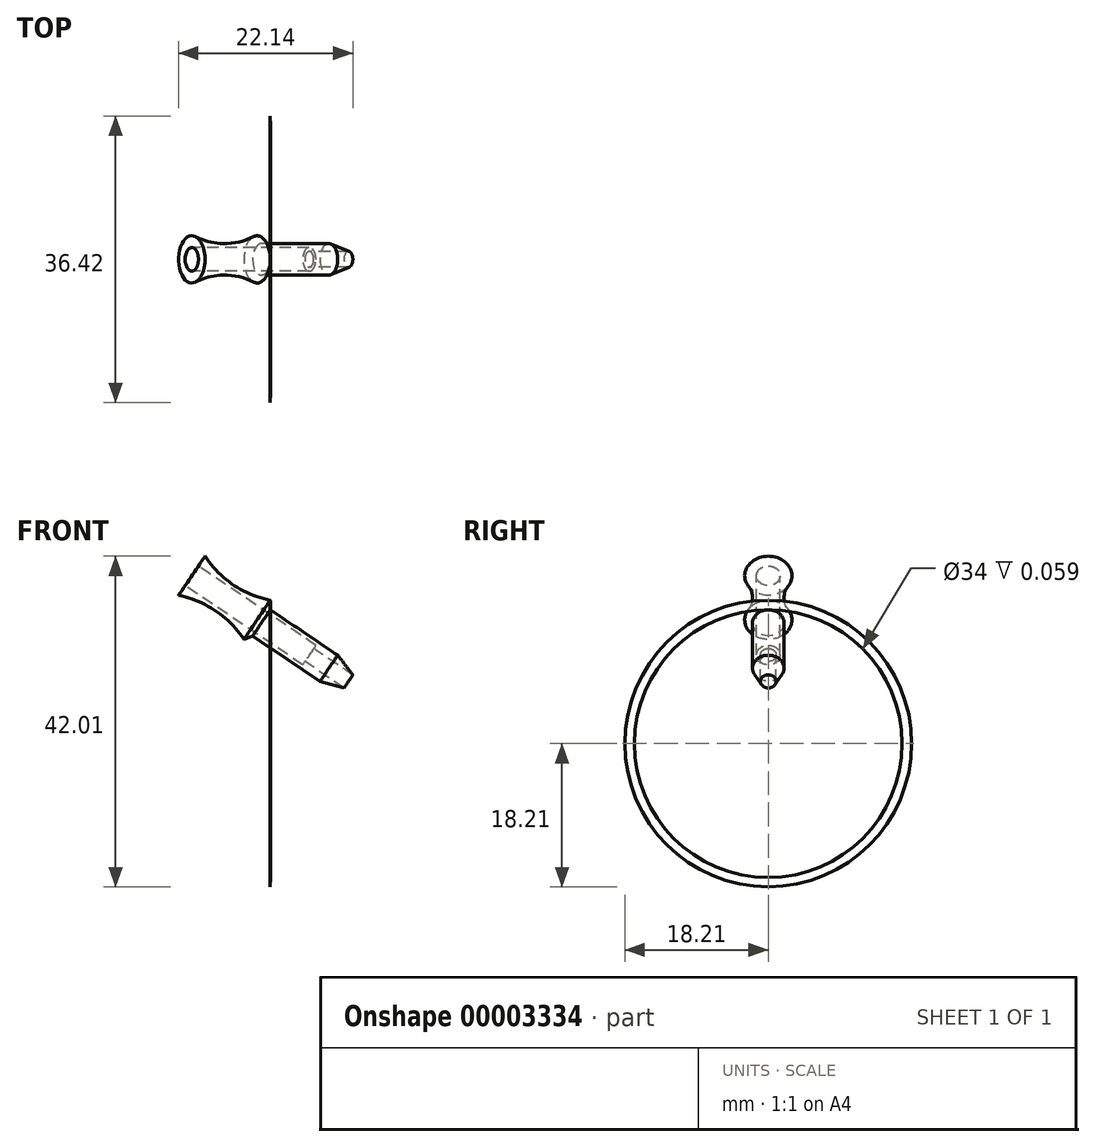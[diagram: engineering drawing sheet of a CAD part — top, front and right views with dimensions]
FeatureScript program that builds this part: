
annotation { "Feature Type Name" : "Feature", "Feature Type Description" : "" }
export const myFeature = defineFeature(function(context is Context, id is Id, definition is map)
    precondition{}
    {
        {
            var Q0;
            Q0=qCreatedBy(makeId("Front.planeOp"),FACE);
            var sketch = newSketch(context, id + "F0", { "sketchPlane" : qUnion([Q0])});
            skLineSegment(sketch, "E0", {"start": v(0, 0) * mm, "end": v(7.5, 0) * mm, "construction": true});
            skLineSegment(sketch, "E1", {"start": v(0, 17) * mm, "end": v(0, 20.5) * mm});
            skLineSegment(sketch, "E2", {"start": v(0, 20.5) * mm, "end": v(7.5, 20.5) * mm});
            skLineSegment(sketch, "E3.0.MirrorCS", {"start": v(0, -17) * mm, "end": v(0, -20.5) * mm});
            skLineSegment(sketch, "E4.0.MirrorCS", {"start": v(0, -20.5) * mm, "end": v(7.5, -20.5) * mm});
            skLineSegment(sketch, "E5.0", {"start": v(1.5, 18.9) * mm, "end": v(7.5, 18.9) * mm});
            skLineSegment(sketch, "E5.1", {"start": v(1.5, 17) * mm, "end": v(1.5, 18.9) * mm});
            skLineSegment(sketch, "E6.0.MirrorCS", {"start": v(1.5, -17) * mm, "end": v(1.5, -18.9) * mm});
            skLineSegment(sketch, "E7.0.MirrorCS", {"start": v(1.5, -18.9) * mm, "end": v(7.5, -18.9) * mm});
            skLineSegment(sketch, "E8", {"start": v(0, 17) * mm, "end": v(1.5, 17) * mm});
            skLineSegment(sketch, "E9", {"start": v(7.5, 20.5) * mm, "end": v(7.5, 18.9) * mm});
            skLineSegment(sketch, "E10.0.MirrorCS", {"start": v(0, -17) * mm, "end": v(1.5, -17) * mm});
            skLineSegment(sketch, "E11.0.MirrorCS", {"start": v(7.5, -20.5) * mm, "end": v(7.5, -18.9) * mm});
            skLineSegment(sketch, "E12", {"start": v(-9.97, 21.31) * mm, "end": v(10, 7.84) * mm, "construction": true});
            skLineSegment(sketch, "E13", {"start": v(-9.13, 22.55) * mm, "end": v(-8.3, 23.8) * mm});
            skLineSegment(sketch, "E14", {"start": v(0, 18.2) * mm, "end": v(0, 17) * mm});
            skLineSegment(sketch, "E15", {"start": v(0, 17) * mm, "end": v(8.56, 11.23) * mm});
            skLineSegment(sketch, "E16", {"start": v(8.56, 11.23) * mm, "end": v(10.49, 8.72) * mm});
            skLineSegment(sketch, "E17", {"start": v(-9.13, 22.55) * mm, "end": v(5.8, 12.49) * mm});
            skArc(sketch, "E18", {"start": v(-8.3, 23.8) * mm, "mid": v(-4.7, 20.17) * mm, "end": v(0, 18.2) * mm});
            skLineSegment(sketch, "E19", {"start": v(-8.3, 23.8) * mm, "end": v(0, 18.2) * mm, "construction": true});
            skLineSegment(sketch, "E20", {"start": v(8.56, 11.23) * mm, "end": v(8, 10.4) * mm, "construction": true});
            skLineSegment(sketch, "E21", {"start": v(10.49, 8.72) * mm, "end": v(5.51, 12.07) * mm});
            skLineSegment(sketch, "E22", {"start": v(5.51, 12.07) * mm, "end": v(5.8, 12.49) * mm});
            skLineSegment(sketch, "E23.0.MirrorCS", {"start": v(9.37, 7.06) * mm, "end": v(4.4, 10.42) * mm});
            skLineSegment(sketch, "E24.0.MirrorCS", {"start": v(6.32, 7.9) * mm, "end": v(9.37, 7.06) * mm});
            skLineSegment(sketch, "E25.0.MirrorCS", {"start": v(-2.24, 13.68) * mm, "end": v(6.32, 7.9) * mm});
            skLineSegment(sketch, "E26.0.MirrorCS", {"start": v(4.12, 10) * mm, "end": v(4.4, 10.42) * mm});
            skLineSegment(sketch, "E27.0.MirrorCS", {"start": v(-10.8, 20.07) * mm, "end": v(4.12, 10) * mm});
            skLineSegment(sketch, "E28.0.MirrorCS", {"start": v(-3.36, 13.23) * mm, "end": v(-2.24, 13.68) * mm});
            skArc(sketch, "E29.0.MirrorCS", {"start": v(-11.65, 18.82) * mm, "mid": v(-6.94, 16.86) * mm, "end": v(-3.36, 13.23) * mm});
            skLineSegment(sketch, "E30.0.MirrorCS", {"start": v(-10.8, 20.07) * mm, "end": v(-11.65, 18.82) * mm});
            skLineSegment(sketch, "E31", {"start": v(0, 18.2) * mm, "end": v(0.06, 16.96) * mm});
            skSolve(sketch);
        }
        {
            var Q0;
            {var subQ3=sQuery(id+"F0.wireOp",EDGE,"E1");Q0=makeQuery(id+"F0.imprint","IMPRINT",FACE,{"disambiguationData":[TD([[makeQuery(id+"F0.imprint","IMPRINT",EDGE,{"derivedFrom":subQ3}),-1.0]])]});}
            var Q1;
            {var subQ3=sQuery(id+"F0.wireOp",EDGE,"E14");Q1=makeQuery(id+"F0.imprint","IMPRINT",FACE,{"disambiguationData":[TD([[makeQuery(id+"F0.imprint","IMPRINT",EDGE,{"derivedFrom":subQ3}),1.0]])]});}
            var Q2;
            Q2=sQuery(id+"F0.wireOp",EDGE,"E0");
            revolve(context, id + "F1", {"entities" : qUnion([Q0, Q1]), "axis" : qUnion([Q2]), "revolveType" : RevolveType.FULL});
        }
        {
            var Q0;
            {var subQ3=sQuery(id+"F0.wireOp",EDGE,"E14");Q0=makeQuery(id+"F0.imprint","IMPRINT",FACE,{"disambiguationData":[TD([[makeQuery(id+"F0.imprint","IMPRINT",EDGE,{"derivedFrom":subQ3}),1.0]])]});}
            var Q1;
            Q1=makeQuery(id+"F0.imprint","IMPRINT",FACE,{"disambiguationData":[TD([[makeQuery(id+"F0.imprint","IMPRINT",EDGE,{"derivedFrom":sQuery(id+"F0.wireOp",EDGE,"E13")}),-1.0]])]});
            var Q2;
            Q2=sQuery(id+"F0.wireOp",EDGE,"E12");
            revolve(context, id + "F2", {"operationType" : NewBodyOperationType.ADD, "entities" : qUnion([Q0, Q1]), "axis" : qUnion([Q2]), "revolveType" : RevolveType.FULL});
        }
    });
